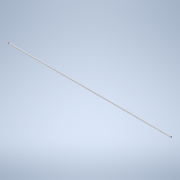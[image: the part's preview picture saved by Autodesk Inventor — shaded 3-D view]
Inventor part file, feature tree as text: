
AUTODESK INVENTOR PART (.ipt)
format: ipt  version: 2022 (Build 260153070, 153G)  size: 91,648 bytes
history: native  units: mm
features: extrude x1, sketch x1
ambient origin geometry x8: Origin, YZ Plane, XZ Plane, XY Plane, X Axis, Y Axis, Z Axis, Center Point
bodies: Solid1 (feature_tree)
feature tree (2):
  extrude  "Extrusion1"  Depth=3000.0mm TaperAngle=0.0deg
  sketch  "Sketch1"  dims[d0=20.0mm d1=3000.0mm d2=0.0mm]
